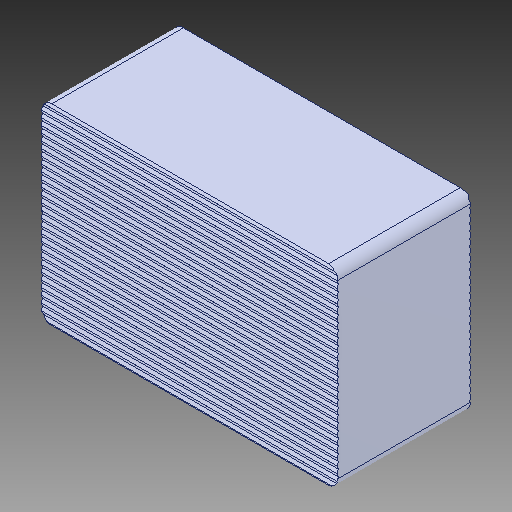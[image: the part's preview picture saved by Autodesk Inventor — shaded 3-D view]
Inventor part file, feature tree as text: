
AUTODESK INVENTOR PART (.ipt)
format: ipt  version: 2018 (Build 220112000, 112)  size: 240,640 bytes
history: native  units: in
note: dims shown in document units (in); Inventor stores cm internally (conversion verified against a paired STEP export)
features: mirror x1
ambient origin geometry x8: Origin, YZ Plane, XZ Plane, XY Plane, X Axis, Y Axis, Z Axis, Center Point
bodies: Solid1 (feature_tree)
feature tree (1):
  mirror  "Mirror1"
